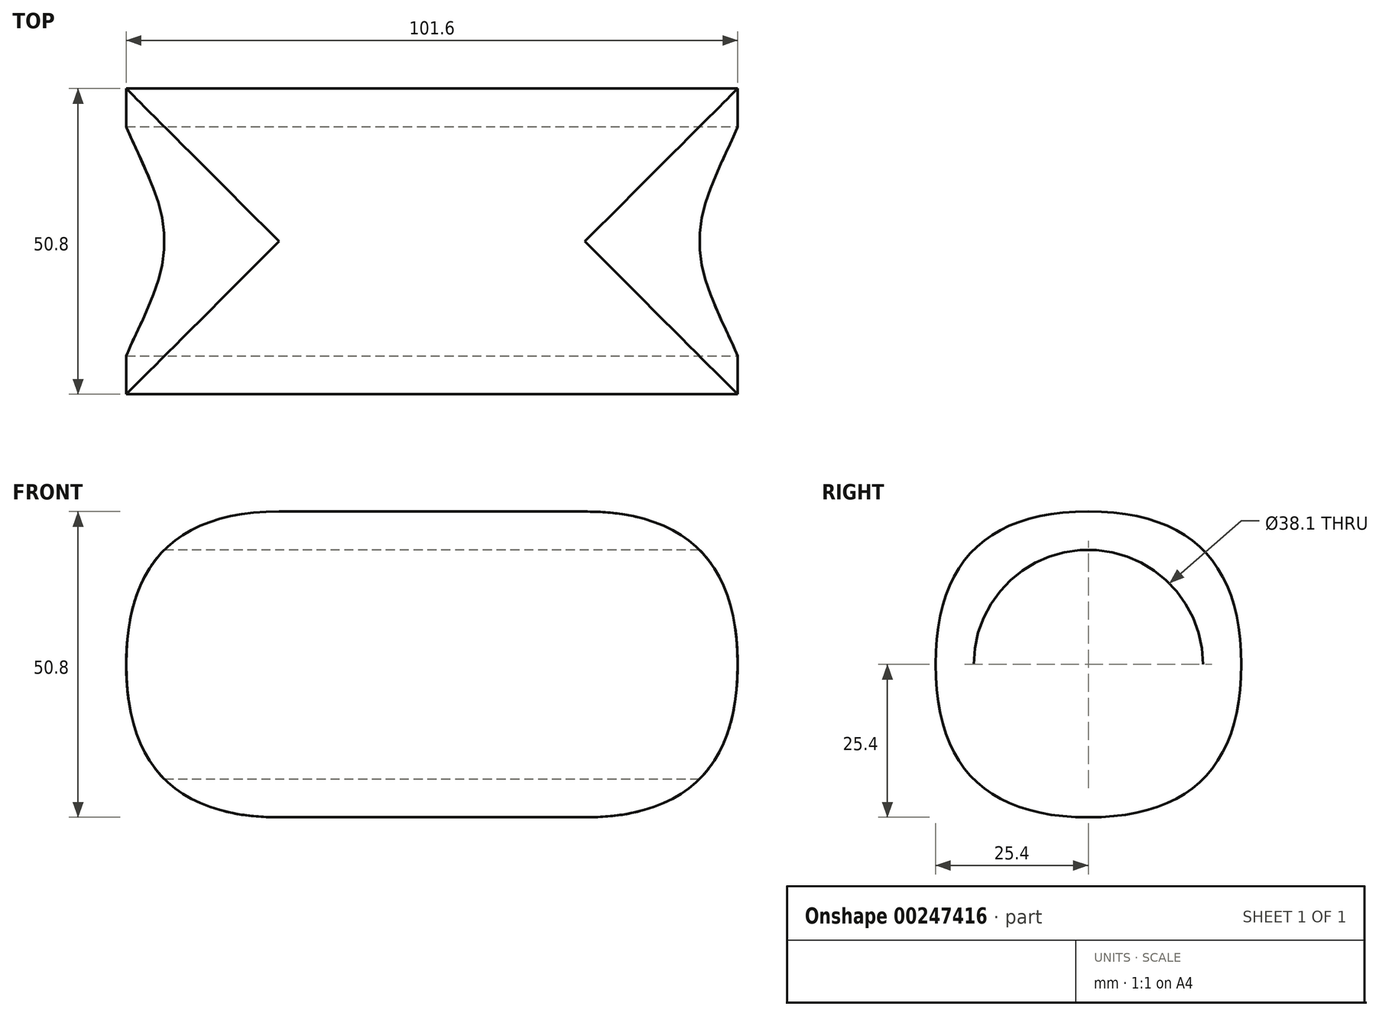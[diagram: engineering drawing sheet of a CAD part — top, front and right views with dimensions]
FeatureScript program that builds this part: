
annotation { "Feature Type Name" : "Feature", "Feature Type Description" : "" }
export const myFeature = defineFeature(function(context is Context, id is Id, definition is map)
    precondition{}
    {
        {
            var Q0;
            Q0=qCreatedBy(makeId("Top.planeOp"),FACE);
            var sketch = newSketch(context, id + "F0", { "sketchPlane" : qUnion([Q0])});
            skLineSegment(sketch, "E0.bottom", {"start": v(50.8, -25.4) * mm, "end": v(-50.8, -25.4) * mm});
            skLineSegment(sketch, "E0.top", {"start": v(50.8, 25.4) * mm, "end": v(-50.8, 25.4) * mm});
            skLineSegment(sketch, "E0.left", {"start": v(50.8, -25.4) * mm, "end": v(50.8, 25.4) * mm});
            skLineSegment(sketch, "E0.right", {"start": v(-50.8, -25.4) * mm, "end": v(-50.8, 25.4) * mm});
            skPoint(sketch, "E0.middle", {"position": v(0, 0) * mm});
            skSolve(sketch);
        }
        {
            var Q0;
            Q0=makeQuery(id+"F0.imprint","IMPRINT",FACE,{"disambiguationData":[TD([[makeQuery(id+"F0.imprint","IMPRINT",EDGE,{"derivedFrom":sQuery(id+"F0.wireOp",EDGE,"E0.bottom")}),-1.0]])]});
            extrude(context, id + "F1", {"entities" : qUnion([Q0]), "depth" : 25.4 * mm});
        }
        {
            var Q0;
            Q0=makeQuery(id+"F1.opExtrude","CAP_EDGE",EDGE,{"disambiguationData":[OSD([sQuery(id+"F0.wireOp",EDGE,"E0.left")])],"isStart":false});
            var Q1;
            Q1=makeQuery(id+"F1.opExtrude","CAP_EDGE",EDGE,{"disambiguationData":[OSD([sQuery(id+"F0.wireOp",EDGE,"E0.top")])],"isStart":false});
            var Q2;
            Q2=makeQuery(id+"F1.opExtrude","CAP_EDGE",EDGE,{"disambiguationData":[OSD([sQuery(id+"F0.wireOp",EDGE,"E0.right")])],"isStart":false});
            var Q3;
            Q3=makeQuery(id+"F1.opExtrude","CAP_EDGE",EDGE,{"disambiguationData":[OSD([sQuery(id+"F0.wireOp",EDGE,"E0.bottom")])],"isStart":false});
            fillet(context, id + "F2", {"entities" : qUnion([Q0, Q1, Q2, Q3]), "radius" : 25.4 * mm, "rho" : 0.5, "crossSection" : FilletCrossSection.CONIC, "allowEdgeOverflow" : false});
        }
        {
            var Q0;
            Q0=makeQuery(id+"F1.opExtrude","SWEPT_BODY",BODY,{"disambiguationData":[OSD([sQuery(id+"F0.wireOp",EDGE,"E0.bottom"),sQuery(id+"F0.wireOp",EDGE,"E0.top"),sQuery(id+"F0.wireOp",EDGE,"E0.left"),sQuery(id+"F0.wireOp",EDGE,"E0.right")])]});
            var Q1;
            Q1=qCreatedBy(makeId("Top.planeOp"),FACE);
            mirror(context, id + "F3", {"operationType" : NewBodyOperationType.ADD, "entities" : qUnion([Q0]), "mirrorPlane" : qUnion([Q1])});
        }
        {
            var Q0;
            Q0=qCreatedBy(makeId("Right.planeOp"),FACE);
            var sketch = newSketch(context, id + "F4", { "sketchPlane" : qUnion([Q0])});
            skCircle(sketch, "E1", {"center": v(0, 0) * mm, "radius": 19.05 * mm});
            skSolve(sketch);
        }
        {
            var Q0;
            Q0 = qSketchRegion(id + "F4", true);
            extrude(context, id + "F5", {"entities" : qUnion([Q0]), "operationType" : NewBodyOperationType.REMOVE, "oppositeDirection" : true, "depth" : 50.8 * mm, "hasSecondDirection" : true, "secondDirectionOppositeDirection" : false, "secondDirectionDepth" : 50.8 * mm});
        }
        {
            var Q0;
            Q0=qCreatedBy(makeId("Front.planeOp"),FACE);
            var sketch = newSketch(context, id + "F6", { "sketchPlane" : qUnion([Q0])});
            skLineSegment(sketch, "E2", {"start": v(0, 0) * mm, "end": v(0, 76.2) * mm, "construction": true});
            skLineSegment(sketch, "E3", {"start": v(0, 76.2) * mm, "end": v(-25.4, 32.2) * mm});
            skLineSegment(sketch, "E4", {"start": v(-25.4, 32.2) * mm, "end": v(0, 32.2) * mm});
            skLineSegment(sketch, "E5", {"start": v(0, 32.2) * mm, "end": v(0, 76.2) * mm});
            skSolve(sketch);
        }
        {
            var Q0;
            Q0=sQuery(id+"F6.wireOp",EDGE,"E3");
            var Q1;
            Q1=sQuery(id+"F6.wireOp",EDGE,"E4");
            var Q2;
            Q2=sQuery(id+"F6.wireOp",EDGE,"E2");
            revolve(context, id + "F7", {"bodyType" : ToolBodyType.SURFACE, "surfaceEntities" : qUnion([Q0, Q1]), "axis" : qUnion([Q2]), "revolveType" : RevolveType.FULL});
        }
    });
